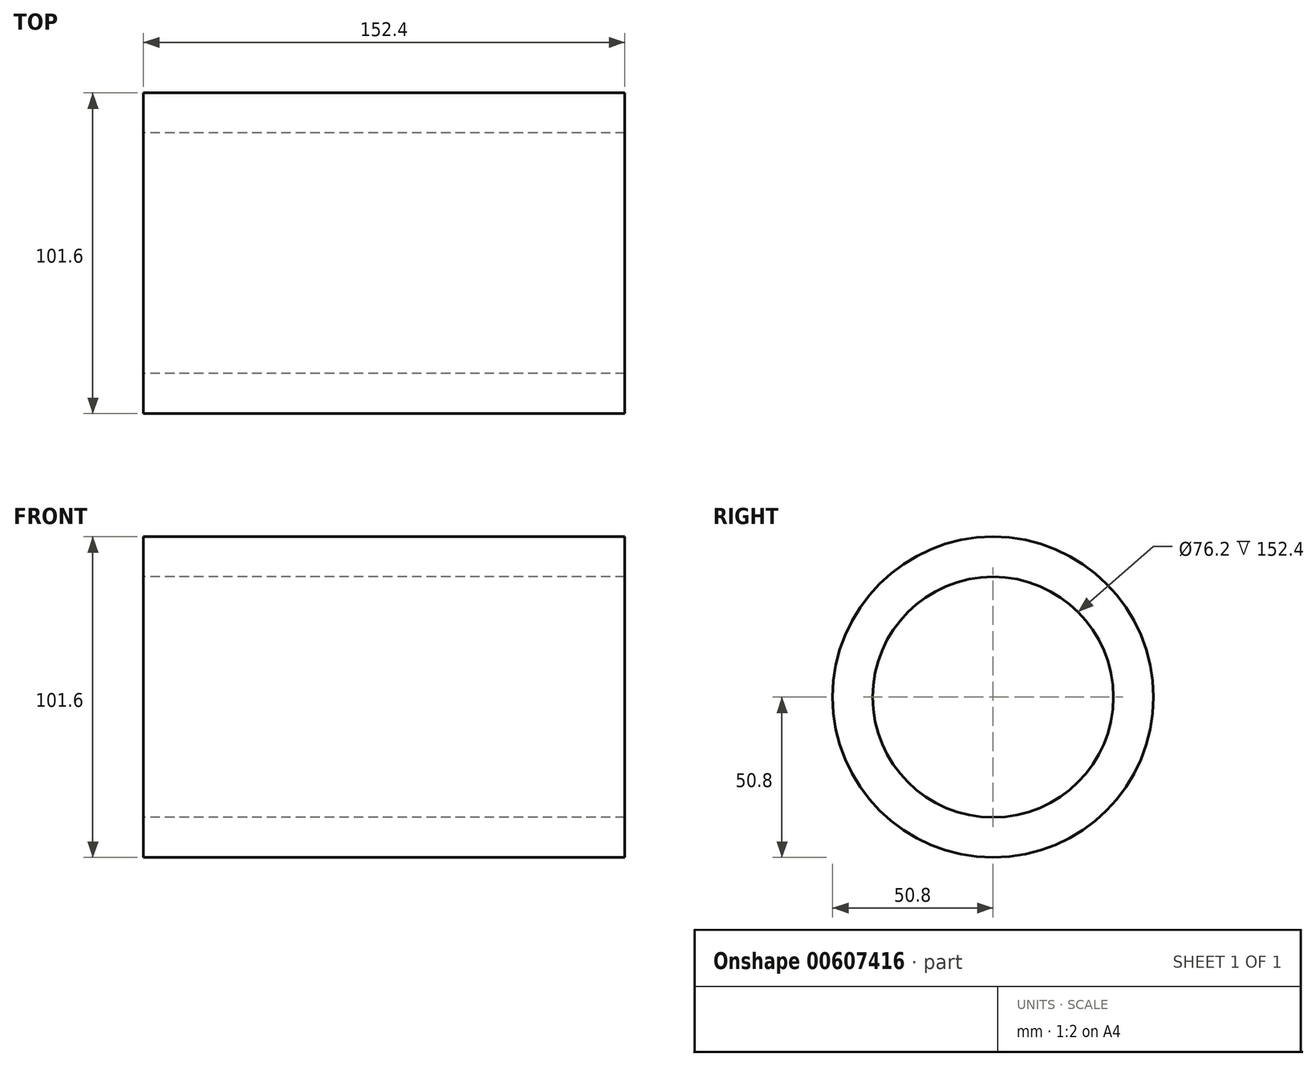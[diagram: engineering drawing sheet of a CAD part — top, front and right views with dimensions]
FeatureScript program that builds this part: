
annotation { "Feature Type Name" : "Feature", "Feature Type Description" : "" }
export const myFeature = defineFeature(function(context is Context, id is Id, definition is map)
    precondition{}
    {
        {
            var Q0;
            Q0=qCreatedBy(makeId("Front.planeOp"),FACE);
            var sketch = newSketch(context, id + "F0", { "sketchPlane" : qUnion([Q0])});
            skLineSegment(sketch, "E0.bottom", {"start": v(0, 50.8) * mm, "end": v(152.4, 50.8) * mm});
            skLineSegment(sketch, "E0.top", {"start": v(0, 38.1) * mm, "end": v(152.4, 38.1) * mm});
            skLineSegment(sketch, "E0.left", {"start": v(0, 50.8) * mm, "end": v(0, 38.1) * mm});
            skLineSegment(sketch, "E0.right", {"start": v(152.4, 50.8) * mm, "end": v(152.4, 38.1) * mm});
            skLineSegment(sketch, "E1", {"start": v(0, 0) * mm, "end": v(145.52, 0) * mm, "construction": true});
            skSolve(sketch);
        }
        {
            var Q0;
            Q0 = qSketchRegion(id + "F0", true);
            var Q1;
            Q1=sQuery(id+"F0.wireOp",EDGE,"E1");
            revolve(context, id + "F1", {"entities" : qUnion([Q0]), "axis" : qUnion([Q1]), "revolveType" : RevolveType.FULL});
        }
    });
